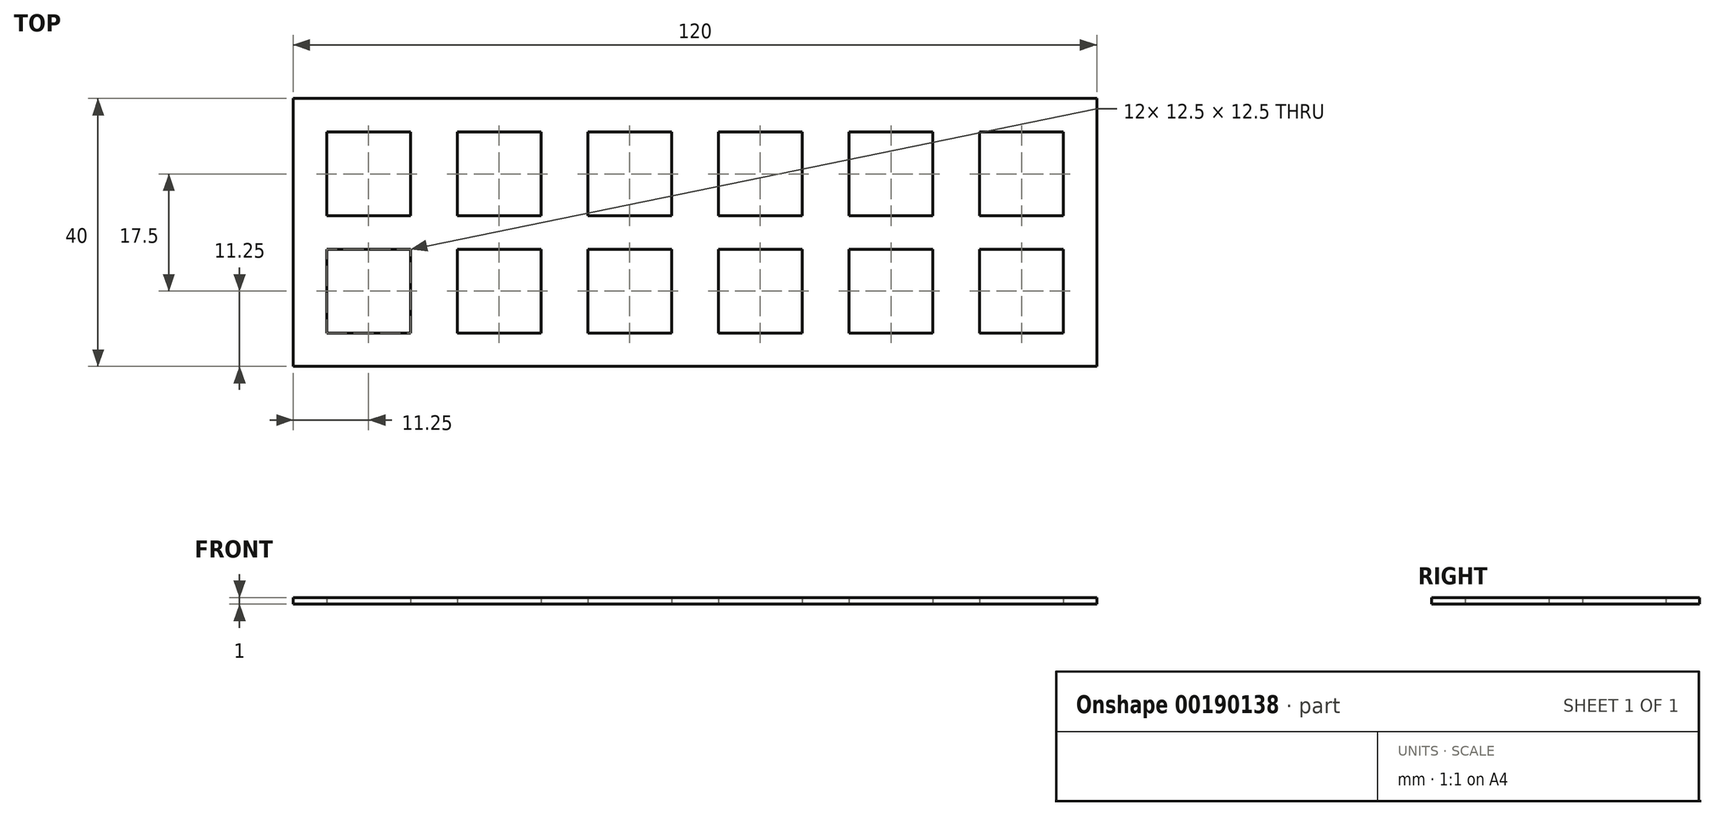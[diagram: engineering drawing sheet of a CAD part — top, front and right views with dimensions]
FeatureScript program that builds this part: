
annotation { "Feature Type Name" : "Feature", "Feature Type Description" : "" }
export const myFeature = defineFeature(function(context is Context, id is Id, definition is map)
    precondition{}
    {
        {
            var Q0;
            Q0=qCreatedBy(makeId("Top.planeOp"),FACE);
            var sketch = newSketch(context, id + "F0", { "sketchPlane" : qUnion([Q0])});
            skLineSegment(sketch, "E0.bottom", {"start": v(60, -20) * mm, "end": v(-60, -20) * mm});
            skLineSegment(sketch, "E0.top", {"start": v(60, 20) * mm, "end": v(-60, 20) * mm});
            skLineSegment(sketch, "E0.left", {"start": v(60, -20) * mm, "end": v(60, 20) * mm});
            skLineSegment(sketch, "E0.right", {"start": v(-60, -20) * mm, "end": v(-60, 20) * mm});
            skLineSegment(sketch, "E1", {"start": v(-55, 2.5) * mm, "end": v(-42.5, 2.5) * mm});
            skLineSegment(sketch, "E2", {"start": v(-42.5, 15) * mm, "end": v(-42.5, 2.5) * mm});
            skLineSegment(sketch, "E3.trimOffspring", {"start": v(-55, 2.5) * mm, "end": v(-55, 15) * mm});
            skLineSegment(sketch, "E4.trimOffspring", {"start": v(-42.5, 15) * mm, "end": v(-55, 15) * mm});
            skLineSegment(sketch, "E5.0.1.0", {"start": v(-42.5, -2.5) * mm, "end": v(-42.5, -15) * mm});
            skLineSegment(sketch, "E5.0.1.1", {"start": v(-55, -15) * mm, "end": v(-55, -2.5) * mm});
            skLineSegment(sketch, "E5.0.1.2", {"start": v(-42.5, -2.5) * mm, "end": v(-55, -2.5) * mm});
            skLineSegment(sketch, "E5.0.1.3", {"start": v(-55, -15) * mm, "end": v(-42.5, -15) * mm});
            skLineSegment(sketch, "E5.1.0.0", {"start": v(-23, 15) * mm, "end": v(-23, 2.5) * mm});
            skLineSegment(sketch, "E5.1.0.1", {"start": v(-35.5, 2.5) * mm, "end": v(-35.5, 15) * mm});
            skLineSegment(sketch, "E5.1.0.2", {"start": v(-23, 15) * mm, "end": v(-35.5, 15) * mm});
            skLineSegment(sketch, "E5.1.0.3", {"start": v(-35.5, 2.5) * mm, "end": v(-23, 2.5) * mm});
            skLineSegment(sketch, "E5.1.1.0", {"start": v(-23, -2.5) * mm, "end": v(-23, -15) * mm});
            skLineSegment(sketch, "E5.1.1.1", {"start": v(-35.5, -15) * mm, "end": v(-35.5, -2.5) * mm});
            skLineSegment(sketch, "E5.1.1.2", {"start": v(-23, -2.5) * mm, "end": v(-35.5, -2.5) * mm});
            skLineSegment(sketch, "E5.1.1.3", {"start": v(-35.5, -15) * mm, "end": v(-23, -15) * mm});
            skLineSegment(sketch, "E5.2.0.0", {"start": v(-3.5, 15) * mm, "end": v(-3.5, 2.5) * mm});
            skLineSegment(sketch, "E5.2.0.1", {"start": v(-16, 2.5) * mm, "end": v(-16, 15) * mm});
            skLineSegment(sketch, "E5.2.0.2", {"start": v(-3.5, 15) * mm, "end": v(-16, 15) * mm});
            skLineSegment(sketch, "E5.2.0.3", {"start": v(-16, 2.5) * mm, "end": v(-3.5, 2.5) * mm});
            skLineSegment(sketch, "E5.2.1.0", {"start": v(-3.5, -2.5) * mm, "end": v(-3.5, -15) * mm});
            skLineSegment(sketch, "E5.2.1.1", {"start": v(-16, -15) * mm, "end": v(-16, -2.5) * mm});
            skLineSegment(sketch, "E5.2.1.2", {"start": v(-3.5, -2.5) * mm, "end": v(-16, -2.5) * mm});
            skLineSegment(sketch, "E5.2.1.3", {"start": v(-16, -15) * mm, "end": v(-3.5, -15) * mm});
            skLineSegment(sketch, "E5.direction1", {"start": v(-55, 2.5) * mm, "end": v(-35.5, 2.5) * mm, "construction": true});
            skLineSegment(sketch, "E5.direction2", {"start": v(-55, 2.5) * mm, "end": v(-55, -15) * mm, "construction": true});
            skLineSegment(sketch, "E6.0.3.0", {"start": v(16, 15) * mm, "end": v(16, 2.5) * mm});
            skLineSegment(sketch, "E6.3.3.0", {"start": v(3.5, 2.5) * mm, "end": v(3.5, 15) * mm});
            skLineSegment(sketch, "E6.6.3.0", {"start": v(16, 15) * mm, "end": v(3.5, 15) * mm});
            skLineSegment(sketch, "E6.9.3.0", {"start": v(3.5, 2.5) * mm, "end": v(16, 2.5) * mm});
            skLineSegment(sketch, "E6.0.3.1", {"start": v(16, -2.5) * mm, "end": v(16, -15) * mm});
            skLineSegment(sketch, "E6.3.3.1", {"start": v(3.5, -15) * mm, "end": v(3.5, -2.5) * mm});
            skLineSegment(sketch, "E6.6.3.1", {"start": v(16, -2.5) * mm, "end": v(3.5, -2.5) * mm});
            skLineSegment(sketch, "E6.9.3.1", {"start": v(3.5, -15) * mm, "end": v(16, -15) * mm});
            skLineSegment(sketch, "E6.0.4.0", {"start": v(35.5, 15) * mm, "end": v(35.5, 2.5) * mm});
            skLineSegment(sketch, "E6.3.4.0", {"start": v(23, 2.5) * mm, "end": v(23, 15) * mm});
            skLineSegment(sketch, "E6.6.4.0", {"start": v(35.5, 15) * mm, "end": v(23, 15) * mm});
            skLineSegment(sketch, "E6.9.4.0", {"start": v(23, 2.5) * mm, "end": v(35.5, 2.5) * mm});
            skLineSegment(sketch, "E6.0.4.1", {"start": v(35.5, -2.5) * mm, "end": v(35.5, -15) * mm});
            skLineSegment(sketch, "E6.3.4.1", {"start": v(23, -15) * mm, "end": v(23, -2.5) * mm});
            skLineSegment(sketch, "E6.6.4.1", {"start": v(35.5, -2.5) * mm, "end": v(23, -2.5) * mm});
            skLineSegment(sketch, "E6.9.4.1", {"start": v(23, -15) * mm, "end": v(35.5, -15) * mm});
            skLineSegment(sketch, "E6.0.5.0", {"start": v(55, 15) * mm, "end": v(55, 2.5) * mm});
            skLineSegment(sketch, "E6.3.5.0", {"start": v(42.5, 2.5) * mm, "end": v(42.5, 15) * mm});
            skLineSegment(sketch, "E6.6.5.0", {"start": v(55, 15) * mm, "end": v(42.5, 15) * mm});
            skLineSegment(sketch, "E6.9.5.0", {"start": v(42.5, 2.5) * mm, "end": v(55, 2.5) * mm});
            skLineSegment(sketch, "E6.0.5.1", {"start": v(55, -2.5) * mm, "end": v(55, -15) * mm});
            skLineSegment(sketch, "E6.3.5.1", {"start": v(42.5, -15) * mm, "end": v(42.5, -2.5) * mm});
            skLineSegment(sketch, "E6.6.5.1", {"start": v(55, -2.5) * mm, "end": v(42.5, -2.5) * mm});
            skLineSegment(sketch, "E6.9.5.1", {"start": v(42.5, -15) * mm, "end": v(55, -15) * mm});
            skSolve(sketch);
        }
        {
            var Q0;
            Q0 = qSketchRegion(id + "F0", true);
            extrude(context, id + "F1", {"entities" : qUnion([Q0]), "depth" : 1 * mm, "offsetDistance" : 25 * mm});
        }
    });
